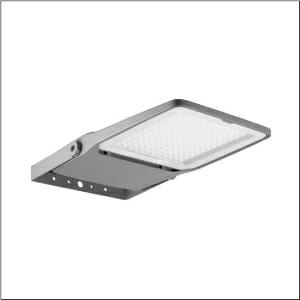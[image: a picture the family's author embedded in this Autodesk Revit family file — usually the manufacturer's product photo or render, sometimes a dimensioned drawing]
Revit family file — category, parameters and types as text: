
# Revit family: floodlight_fl_20_midi___rs17_5xa7682e1b2ac_1478
name_source: partatom
category: Lighting Fixtures
units: mm (PartAtom-declared; Revit-internal decimal feet)

## family parameters
Cut with Voids When Loaded = No
Host = Face
Light Source = No
Part Type = Normal
Room Calculation Point = No
Round Connector Dimension = Use Diameter
Shared = No

## types (1)
- --- (1 x LED 3000K / CRI = 80 (unbekannt), 22840 lm, 3000K)
    Apparent Load = 208 VA
    CIE Flux Codes = 79 92 99 100 100
    Color Rendering = 80
    Color Temperature = 3000K
    Default Elevation = 1800 mm
    Description = Floodlight FL 20 midi, floodlight, primary light control with lens, of plastic, primary optical cover: protective disc, of toughened safety glass, transparent, light distribution: RS17, light emission: direct distribution, primary light characteristic: rotationally symmetric, installation type: surface-mounted, LED, High Power LED, rated luminous flux: 22.840lm, luminous efficacy: 110lm/W, light colour: 830, colour temperature: 3000K, control gear: ECG Plus, control: flexible luminous flux parameterisation, time-dependent luminous flux control, digital communication interface, power reduction, overheat protection, electronic power reduction, with terminal, 5-pole, max. 2.5mm², mains connection: 220..240V, AC, 50/60Hz, rated input power: 208W, LED unit, of diecast aluminium, powder-coated, Siteco® metallic grey (DB 702S), corrosivity category C5 mid according to DIN EN ISO 12944, incl. 1x M20 cable gland for cable Ø 6.5..12mm, length: 731mm, width: 450mm, height: 76mm, housing frame, of diecast aluminium, powder-coated, Siteco® metallic grey (DB 702S), wall fastening, of steel, powder-coated, Siteco® metallic grey (DB 702S), DALI, protection rating (complete): IP66, insulation class (complete): insulation class II (safety insulation), certification: CE, ENEC, VDE, protection symbol: D, permissible operating ambient temperature: -40..+40°C, permissible operating ambient temperature for outdoor applications: -40..+50°C, standard: DIN EN 12944, packaging unit: 1 piece

Light Distribution: RS17
    Height = 76 mm
    Lamp = 1 x LED 3000K / CRI >= 80 (unbekannt)
    Lamp Light Flux = 22840 lm
    Lamp count = 1
    Length = 731 mm
    Luminous efficacy = 110 lm/W
    Manufacturer = Siteco
    ModVariant = No
    Model = 5XA7682E1B2AC
    Mounting Place = Wall
    Mounting Type = Surface mounted
    Number of Poles = 1
    OnlyDefault = Yes
    Power Factor = 1
    Product Name = Floodlight FL 20 midi | RS17
    Product group = floodlight | wall mounted
    ProductGroupID = 2001
    Protection Class = Protection class II
    Protection Degree = IP 66
    RLX_Detail_Level = 1
    RLX_Emergency_Light_Flux = 0 lm
    RLX_Emergency_Type = 0
    RLX_Emergency_Type_DB = No
    RlxData = <blob elided: 86665 chars, md5=43b7711b>
    Socket = socket
    Standby Power = 0 W
    System Light Flux = 22840 lm
    System Power = 208 W
    Type Comments = factory setting: luminous flux: 100 % | dim-lin: 254 | 484 mA
    Type Image = l_1005944.jpg
    URL = http://relux.com
    VarID = @adj_146485
    Voltage = 0 V
    Weight = 0.00 kg
    Width = 450 mm

## geometry (parser evidence)
native form markers: Blend x4, Sweep x11
no freeform markers — native parametric forms only
